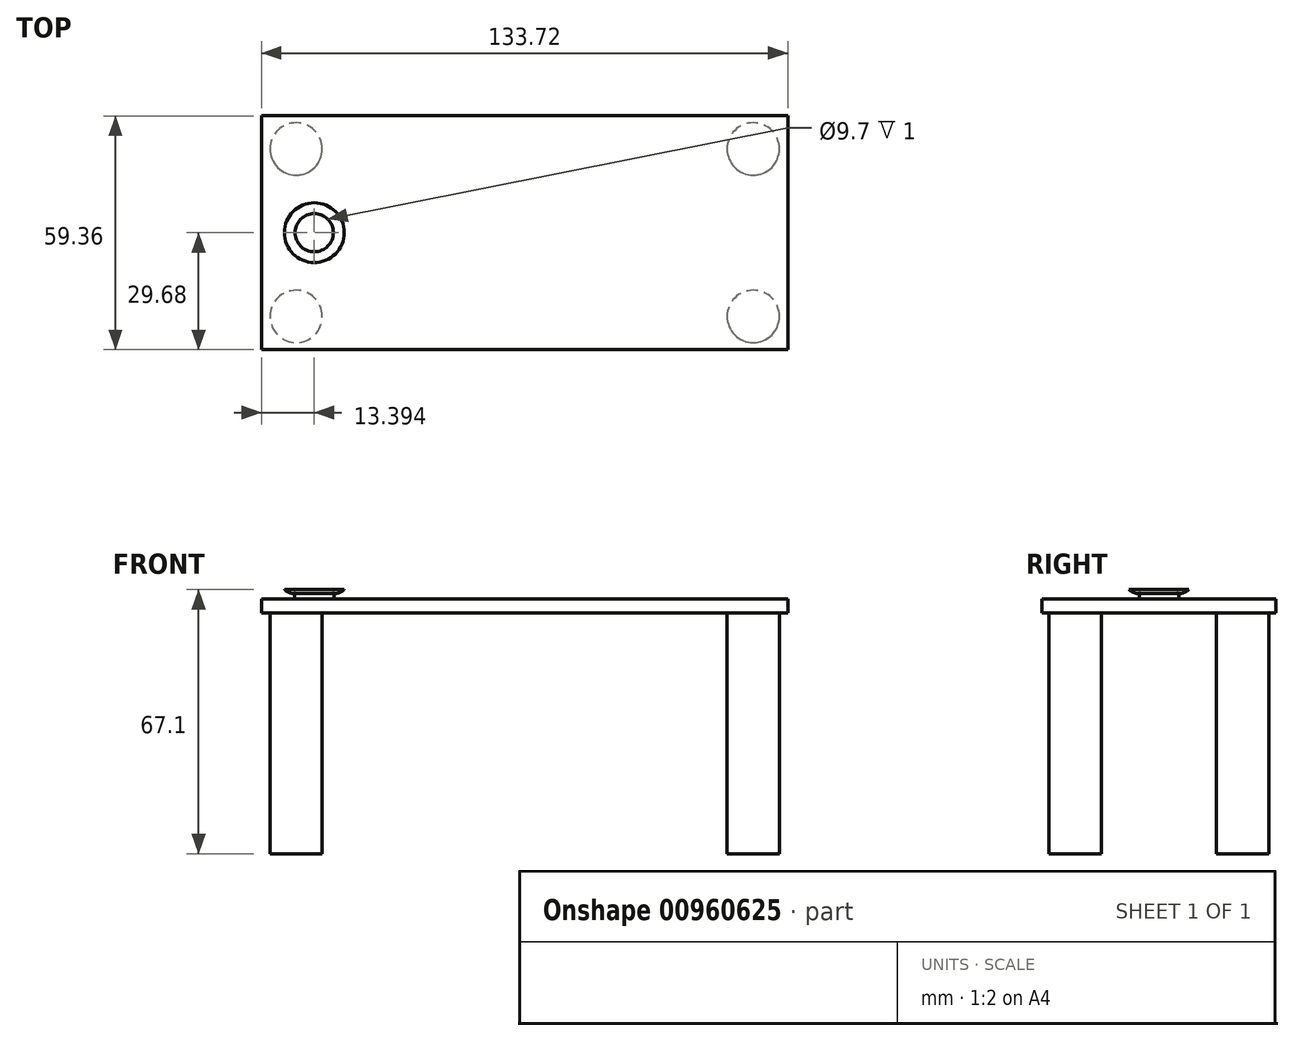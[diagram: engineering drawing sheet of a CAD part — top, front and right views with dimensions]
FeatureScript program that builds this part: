
annotation { "Feature Type Name" : "Feature", "Feature Type Description" : "" }
export const myFeature = defineFeature(function(context is Context, id is Id, definition is map)
    precondition{}
    {
        {
            var Q0;
            Q0=qCreatedBy(makeId("Top.planeOp"),FACE);
            var sketch = newSketch(context, id + "F0", { "sketchPlane" : qUnion([Q0])});
            skLineSegment(sketch, "E0.bottom", {"start": v(-66.86, 29.68) * mm, "end": v(66.86, 29.68) * mm});
            skLineSegment(sketch, "E0.top", {"start": v(-66.86, -29.68) * mm, "end": v(66.86, -29.68) * mm});
            skLineSegment(sketch, "E0.left", {"start": v(-66.86, 29.68) * mm, "end": v(-66.86, -29.68) * mm});
            skLineSegment(sketch, "E0.right", {"start": v(66.86, 29.68) * mm, "end": v(66.86, -29.68) * mm});
            skPoint(sketch, "E0.middle", {"position": v(0, 0) * mm});
            skSolve(sketch);
        }
        {
            var Q0;
            Q0 = qSketchRegion(id + "F0", true);
            extrude(context, id + "F1", {"entities" : qUnion([Q0]), "depth" : 3.5 * mm, "offsetDistance" : 25 * mm});
        }
        {
            var Q0;
            Q0=makeQuery(id+"F1.opExtrude","CAP_FACE",FACE,{"disambiguationData":[OSD([sQuery(id+"F0.wireOp",EDGE,"E0.bottom"),sQuery(id+"F0.wireOp",EDGE,"E0.top"),sQuery(id+"F0.wireOp",EDGE,"E0.left"),sQuery(id+"F0.wireOp",EDGE,"E0.right")])],"isStart":true});
            var sketch = newSketch(context, id + "F2", { "sketchPlane" : qUnion([Q0])});
            skCircle(sketch, "E1", {"center": v(-58.06, 21.29) * mm, "radius": 6.64 * mm});
            skCircle(sketch, "E2.MirrorC", {"center": v(-58.06, -21.29) * mm, "radius": 6.64 * mm});
            skCircle(sketch, "E3.MirrorC", {"center": v(58.06, 21.29) * mm, "radius": 6.64 * mm});
            skCircle(sketch, "E4.MirrorC", {"center": v(58.06, -21.29) * mm, "radius": 6.64 * mm});
            skSolve(sketch);
        }
        {
            var Q0;
            Q0 = qSketchRegion(id + "F2", true);
            extrude(context, id + "F3", {"entities" : qUnion([Q0]), "operationType" : NewBodyOperationType.ADD, "depth" : 61.2 * mm, "offsetDistance" : 25 * mm});
        }
        {
            var Q0;
            Q0=makeQuery(id+"F1.opExtrude","CAP_FACE",FACE,{"disambiguationData":[OSD([sQuery(id+"F0.wireOp",EDGE,"E0.bottom"),sQuery(id+"F0.wireOp",EDGE,"E0.top"),sQuery(id+"F0.wireOp",EDGE,"E0.left"),sQuery(id+"F0.wireOp",EDGE,"E0.right")])],"isStart":false});
            var sketch = newSketch(context, id + "F4", { "sketchPlane" : qUnion([Q0])});
            skCircle(sketch, "E5", {"center": v(-53.47, 0) * mm, "radius": 5 * mm});
            skCircle(sketch, "E6", {"center": v(-53.47, 0) * mm, "radius": 7 * mm});
            skSolve(sketch);
        }
        {
            var Q0;
            Q0=makeQuery(id+"F4.imprint","IMPRINT",FACE,{"disambiguationData":[TD([[makeQuery(id+"F4.imprint","IMPRINT",EDGE,{"derivedFrom":sQuery(id+"F4.wireOp",EDGE,"E5")}),1.0]])]});
            extrude(context, id + "F5", {"entities" : qUnion([Q0]), "operationType" : NewBodyOperationType.ADD, "depth" : 1.4 * mm, "offsetDistance" : 25 * mm});
        }
        {
            var Q0;
            Q0=makeQuery(id+"F5.opExtrude","CAP_FACE",FACE,{"disambiguationData":[OSD([sQuery(id+"F4.wireOp",EDGE,"E5")])],"isStart":false});
            var sketch = newSketch(context, id + "F6", { "sketchPlane" : qUnion([Q0])});
            skCircle(sketch, "E7", {"center": v(-53.47, 0) * mm, "radius": 7.6 * mm});
            skSolve(sketch);
        }
        {
            var Q0;
            Q0 = qSketchRegion(id + "F6", true);
            extrude(context, id + "F7", {"entities" : qUnion([Q0]), "operationType" : NewBodyOperationType.ADD, "depth" : 1 * mm, "offsetDistance" : 25 * mm});
        }
        {
            var Q0;
            Q0=makeQuery(id+"F7.opExtrude","CAP_EDGE",EDGE,{"disambiguationData":[OSD([sQuery(id+"F6.wireOp",EDGE,"E7")])],"isStart":true});
            fillet(context, id + "F8", {"entities" : qUnion([Q0]), "radius" : 3.62 * mm, "tangentPropagation" : true, "allowEdgeOverflow" : false});
        }
        {
            var Q0;
            Q0=makeQuery(id+"F7.opExtrude","CAP_FACE",FACE,{"disambiguationData":[OSD([sQuery(id+"F6.wireOp",EDGE,"E7")])],"isStart":false});
            var sketch = newSketch(context, id + "F9", { "sketchPlane" : qUnion([Q0])});
            skCircle(sketch, "E8", {"center": v(-53.47, 0) * mm, "radius": 4.85 * mm});
            skSolve(sketch);
        }
        {
            var Q0;
            Q0 = qSketchRegion(id + "F9", true);
            extrude(context, id + "F10", {"entities" : qUnion([Q0]), "operationType" : NewBodyOperationType.REMOVE, "oppositeDirection" : true, "depth" : 1 * mm, "offsetDistance" : 25 * mm});
        }
    });
